# Revit family: MBS_closet with drawer
name_source: partatom
category: Generic Models
revit_build: Autodesk Revit 2014 (Build: 20130308_1515(x64)
units: mm (PartAtom-declared; Revit-internal decimal feet)

## types (4) — shared parameters
c_clos back pan height = 820 mm  [stored 2.69029 ft]
c_clos side pan height = 820 mm  [stored 2.69029 ft]
c_draw side height = 360 mm  [stored 1.1811 ft]
c_drawer front height = 390 mm  [stored 1.27953 ft]
panel thickness = 30 mm  [stored 0.0984252 ft]

## per-type parameters (varying)
| type | c_clos back pan widht | c_clos bas pan depht | c_clos bas pan widht | c_clos side panel depht | c_darw bott depht | c_draw bott widht | c_drawer front widht | c_drawer side widht | c_top depht | c_top widht | closet material | top material | top thickness |
| bathroom closet | 700 mm  [stored 2.29659 ft] | 490 mm  [stored 1.60761 ft] | 640 mm  [stored 2.09974 ft] | 490 mm  [stored 1.60761 ft] | 490 mm  [stored 1.60761 ft] | 580 mm  [stored 1.90289 ft] | 700 mm  [stored 2.29659 ft] | 490 mm  [stored 1.60761 ft] | 550 mm | 700 mm  [stored 2.29659 ft] | Oak, White BATHROOM CLOSET MBS | Granite, Cut, Polished CLOSET TOP MBS | 50 mm  [stored 0.164042 ft] |
| kitchen closet | 600 mm | 540 mm  [stored 1.77165 ft] | 540 mm  [stored 1.77165 ft] | 540 mm  [stored 1.77165 ft] | 540 mm  [stored 1.77165 ft] | 480 mm  [stored 1.5748 ft] | 600 mm | 540 mm  [stored 1.77165 ft] | 600 mm | 600 mm | Walnut CLOSET KICTHEN MBS | Granite, Cut, Polished CLOSET TOP MBS | 30 mm  [stored 0.0984252 ft] |
| kichen closet for stool | 600 mm | 540 mm  [stored 1.77165 ft] | 540 mm  [stored 1.77165 ft] | 540 mm  [stored 1.77165 ft] | 540 mm  [stored 1.77165 ft] | 480 mm  [stored 1.5748 ft] | 600 mm | 540 mm  [stored 1.77165 ft] | 900 mm  [stored 2.95276 ft] | 600 mm | Walnut CLOSET KICTHEN MBS | Granite, Cut, Polished CLOSET TOP MBS | 30 mm  [stored 0.0984252 ft] |
| kitchen closet cookers | 600 mm | 540 mm  [stored 1.77165 ft] | 540 mm  [stored 1.77165 ft] | 540 mm  [stored 1.77165 ft] | 540 mm  [stored 1.77165 ft] | 480 mm  [stored 1.5748 ft] | 600 mm | 540 mm  [stored 1.77165 ft] | 600 mm | 600 mm | Walnut CLOSET KICTHEN MBS | Roofing, EPDM Membrane COOKERS MBS | 30 mm  [stored 0.0984252 ft] |

note: [stored X ft] marks values corroborated as IEEE doubles in the binary element streams (Revit-internal decimal feet)

## geometry (parser evidence)
native form markers: Sweep x1
no freeform markers — native parametric forms only
